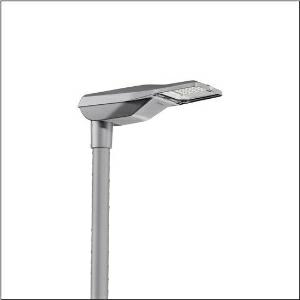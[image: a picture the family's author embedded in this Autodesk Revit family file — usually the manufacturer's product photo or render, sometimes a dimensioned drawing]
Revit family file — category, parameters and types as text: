
# Revit family: streetlight_sl_21_iq_micro___p0_8a_5xe1u31d08cb_216c
name_source: partatom
category: Lighting Fixtures
units: mm (PartAtom-declared; Revit-internal decimal feet)

## family parameters
Cut with Voids When Loaded = No
Host = Face
Light Source = No
Part Type = Normal
Room Calculation Point = No
Round Connector Dimension = Use Diameter
Shared = No

## types (1)
- --- (1 x LED, 2830 lm, 19.4 W, 3000K)
    Apparent Load = 19 VA
    CIE Flux Codes = 33 69 96 100 100
    Color Rendering = 70
    Color Temperature = 3000K
    Default Elevation = 1800 mm
    Description = Streetlight SL 21 iQ micro, mast luminaire, primary light control with lens, of PMMA, primary optical cover: cover, of toughened safety glass, transparent, light distribution: P0.8a, light emission: direct distribution, primary light characteristic: asymmetric, installation type: post-top, side-entry, LED, High Power LED, rated luminous flux: 2.830lm, luminous efficacy: 146lm/W, light colour: 730, colour temperature: 3000K, control gear: iQ-Comfort, control: pre-setting: linear dimming characteristic, Auto-Match, Temp-Guard, Lumen-Switch, Night-Set, Smart-Wire, Light-Fading, Desk-Remote (wireless, voltage-free reading and setting of iQ features in the workshop via application-optimized NFC function/RFID function), optimised constant luminous flux control (CLO 2.0), mains connection: 220..240V, AC, 50/60Hz, start of lifetime: 19W, end of service life: 20W, reduction: 10W, luminaire housing, of diecast aluminium, powder-coated, Siteco® metallic grey (DB 702S), corrosivity category C5 mid according to DIN EN ISO 12944, please order mast flange separately, inclination adjustable: 0°, 5°, 10°, 15°, sealing non-destructively replaceable, multi-level sealing system, length: 528mm, width: 235mm, height: 110mm, mast flange for spigot size: 42mm (side-entry): 5XC10008XM4, 60/48mm (side-entry/post-top): 5XC10108XM2, 76/60mm (side-entry/post-top): 5XC10108XM1, protection rating (complete): IP66, insulation class (complete): insulation class II (safety insulation), certification: CE, ENEC, ENEC+, VDE, impact resistance: IK10, permissible operating ambient temperature for outdoor applications: -40..+50°C, standard-compliant lighting for roads and squares, packaging unit: 1 piece

Light Distribution: P0.8a
    Height = 110 mm
    Lamp = 1 x LED
    Lamp Light Flux = 2830 lm
    Lamp Power = 19.4 W
    Lamp count = 1
    Length = 528 mm
    Luminous efficacy = 146 lm/W
    Manufacturer = Siteco
    ModVariant = No
    Model = 5XE1U31D08CB
    Number of Poles = 1
    OnlyDefault = Yes
    Power Factor = 1
    Product Name = Streetlight SL 21 iQ micro | P0.8a
    Product group = mast luminaire | pylon top
    ProductGroupID = 6100
    Protection Class = Protection class II
    Protection Degree = IP 66
    RLX_Detail_Level = 1
    RLX_Emergency_Light_Flux = 0 lm
    RLX_Emergency_Type = 0
    RLX_Emergency_Type_DB = No
    RlxData = <blob elided: 98537 chars, md5=b6f1e020>
    Socket = socket
    Standby Power = 0 W
    System Light Flux = 2830 lm
    System Power = 19 W
    Type Comments = factory setting: luminous flux: 100 % | dim-lin: 254 | 387 mA
    Type Image = l_1006881.jpg
    URL = http://relux.com
    VarID = @adj_073040
    Voltage = 0 V
    Weight = 0.00 kg
    Width = 235 mm

## geometry (parser evidence)
native form markers: Blend x4, Sweep x10
no freeform markers — native parametric forms only
